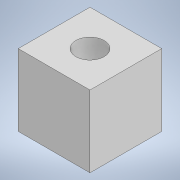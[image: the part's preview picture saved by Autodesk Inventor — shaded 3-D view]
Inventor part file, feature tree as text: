
AUTODESK INVENTOR PART (.ipt)
format: ipt  version: 2020 (Build 240168000, 168)  size: 90,624 bytes
history: native  units: mm
features: extrude x1, sketch x1
ambient origin geometry x8: Origin, YZ Plane, XZ Plane, XY Plane, X Axis, Y Axis, Z Axis, Center Point
bodies: Solid1 (feature_tree)
feature tree (2):
  extrude  "Extrusion1"  Depth=15.0mm
  sketch  "Sketch1"  dims[d0=15.0mm d1=15.0mm d2=5.9mm d3=15.0mm d4=0.0mm]
